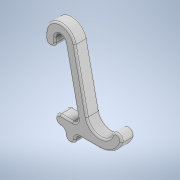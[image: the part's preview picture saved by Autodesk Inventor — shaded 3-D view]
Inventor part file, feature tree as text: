
AUTODESK INVENTOR PART (.ipt)
format: ipt  version: 2020 (Build 240168000, 168)  size: 221,184 bytes
history: native  units: in
note: dims shown in document units (in); Inventor stores cm internally (conversion verified against a paired STEP export)
features: extrude x1, fillet x1, sketch x1
ambient origin geometry x8: Origin, YZ Plane, XZ Plane, XY Plane, X Axis, Y Axis, Z Axis, Center Point
bodies: Solid1 (feature_tree)
feature tree (3):
  extrude  "Extrusion1"  Depth=3.0in
  fillet  "Fillet1"  Radius=1.0994in
  sketch  "Sketch1"  dims[d0=0.375in d7=3.0in d10=1.0994in d12=1.5in d13=1.0in d14=0.5in d15=0.0in d16=0.0625in d17=1.0in]
